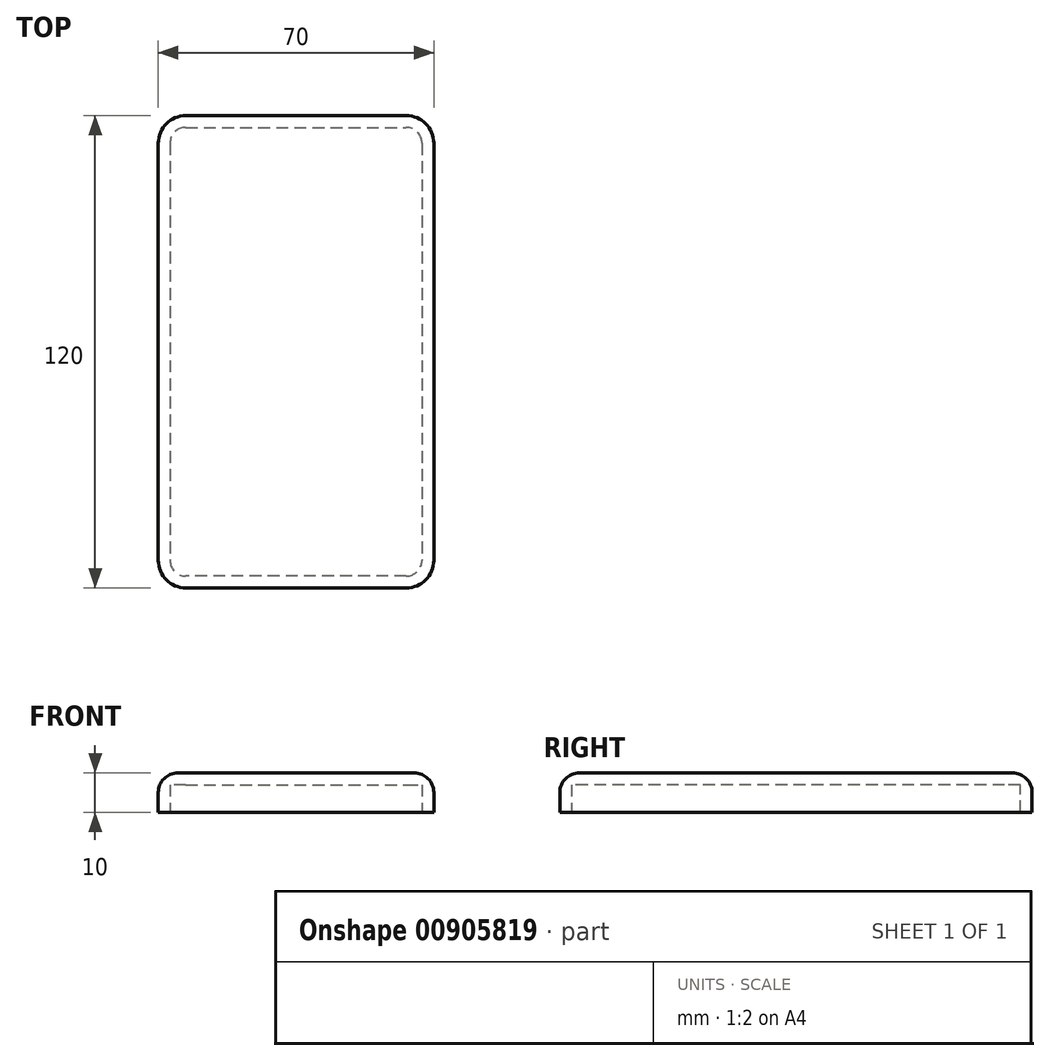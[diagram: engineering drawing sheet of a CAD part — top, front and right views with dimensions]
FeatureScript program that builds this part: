
annotation { "Feature Type Name" : "Feature", "Feature Type Description" : "" }
export const myFeature = defineFeature(function(context is Context, id is Id, definition is map)
    precondition{}
    {
        {
            var Q0;
            Q0=qCreatedBy(makeId("Top.planeOp"),FACE);
            var sketch = newSketch(context, id + "F0", { "sketchPlane" : qUnion([Q0])});
            skLineSegment(sketch, "E0", {"start": v(-35, 53) * mm, "end": v(-35, 0) * mm});
            skLineSegment(sketch, "E1", {"start": v(0, 60) * mm, "end": v(-28, 60) * mm});
            skLineSegment(sketch, "E2", {"start": v(0, 60) * mm, "end": v(28, 60) * mm});
            skLineSegment(sketch, "E3", {"start": v(28, -60) * mm, "end": v(-28, -60) * mm});
            skLineSegment(sketch, "E4", {"start": v(35, 53) * mm, "end": v(35, 0) * mm});
            skLineSegment(sketch, "E5", {"start": v(35, 0) * mm, "end": v(35, -53) * mm});
            skLineSegment(sketch, "E6", {"start": v(-35, 0) * mm, "end": v(-35, -53) * mm});
            skArc(sketch, "E7", {"start": v(-28, 60) * mm, "mid": v(-32.95, 57.95) * mm, "end": v(-35, 53) * mm});
            skArc(sketch, "E8", {"start": v(35, 53) * mm, "mid": v(32.95, 57.95) * mm, "end": v(28, 60) * mm});
            skArc(sketch, "E9", {"start": v(28, -60) * mm, "mid": v(32.95, -57.95) * mm, "end": v(35, -53) * mm});
            skArc(sketch, "E10", {"start": v(-35, -53) * mm, "mid": v(-32.95, -57.95) * mm, "end": v(-28, -60) * mm});
            skSolve(sketch);
        }
        {
            var Q0;
            Q0=qSketchRegion(id+"F0",true);
            extrude(context, id + "F1", {"entities" : qUnion([Q0]), "depth" : 10 * mm, "offsetDistance" : 25 * mm});
        }
        {
            var Q0;
            Q0=makeQuery(id+"F1.opExtrude","CAP_FACE",FACE,{"disambiguationData":[OSD([sQuery(id+"F0.wireOp",EDGE,"E0"),sQuery(id+"F0.wireOp",EDGE,"E1"),sQuery(id+"F0.wireOp",EDGE,"E2"),sQuery(id+"F0.wireOp",EDGE,"E3"),sQuery(id+"F0.wireOp",EDGE,"E4"),sQuery(id+"F0.wireOp",EDGE,"E5"),sQuery(id+"F0.wireOp",EDGE,"E6"),sQuery(id+"F0.wireOp",EDGE,"E7"),sQuery(id+"F0.wireOp",EDGE,"E8"),sQuery(id+"F0.wireOp",EDGE,"E9"),sQuery(id+"F0.wireOp",EDGE,"E10")])],"isStart":true});
            shell(context, id + "F2", {"entities" : qUnion([Q0]), "thickness" : 3 * mm});
        }
        {
            var Q0;
            Q0=makeQuery(id+"F1.opExtrude","CAP_EDGE",EDGE,{"disambiguationData":[OSD([sQuery(id+"F0.wireOp",EDGE,"E7")])],"isStart":false});
            fillet(context, id + "F3", {"entities" : qUnion([Q0]), "radius" : 5 * mm, "tangentPropagation" : true, "allowEdgeOverflow" : false});
        }
    });
